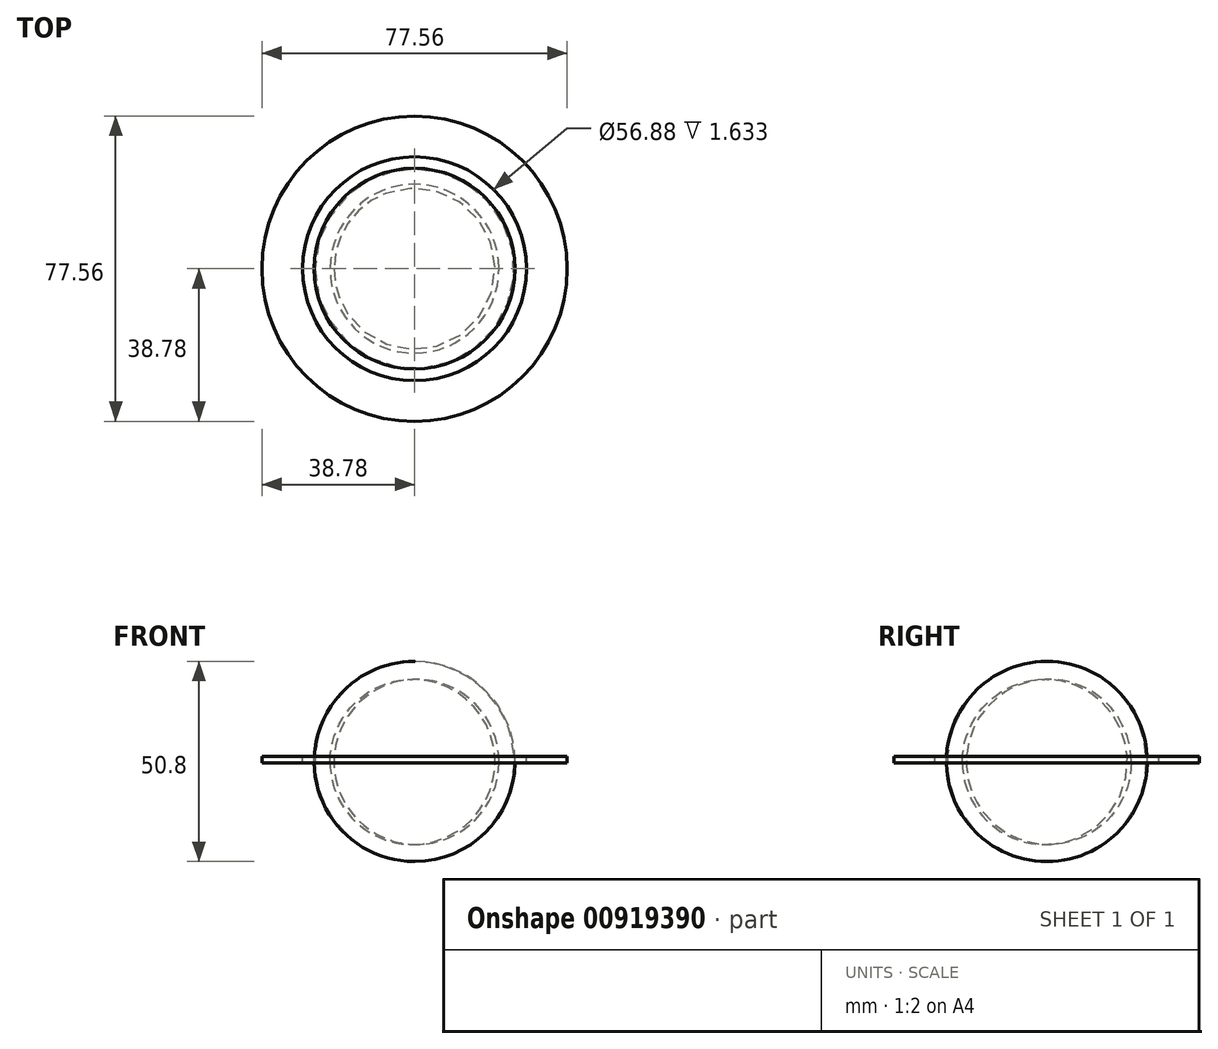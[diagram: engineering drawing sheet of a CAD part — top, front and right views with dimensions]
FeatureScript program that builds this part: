
annotation { "Feature Type Name" : "Feature", "Feature Type Description" : "" }
export const myFeature = defineFeature(function(context is Context, id is Id, definition is map)
    precondition{}
    {
        {
            var Q0;
            Q0=qCreatedBy(makeId("Front.planeOp"),FACE);
            var sketch = newSketch(context, id + "F0", { "sketchPlane" : qUnion([Q0])});
            skArc(sketch, "E0", {"start": v(0, -23.23) * mm, "mid": v(25.29, 2.17) * mm, "end": v(0, 27.57) * mm});
            skLineSegment(sketch, "E1", {"start": v(0, 27.57) * mm, "end": v(0, 23) * mm});
            skLineSegment(sketch, "E2.bottom", {"start": v(38.78, 3.4) * mm, "end": v(28.44, 3.4) * mm});
            skLineSegment(sketch, "E2.top", {"start": v(38.78, 1.77) * mm, "end": v(28.44, 1.77) * mm});
            skLineSegment(sketch, "E2.left", {"start": v(38.78, 3.4) * mm, "end": v(38.78, 1.77) * mm});
            skLineSegment(sketch, "E2.right", {"start": v(28.44, 3.4) * mm, "end": v(28.44, 1.77) * mm});
            skPoint(sketch, "E2.middle", {"position": v(33.6, 2.59) * mm});
            skArc(sketch, "E3", {"start": v(0, -18.91) * mm, "mid": v(20.46, 2.04) * mm, "end": v(0, 23) * mm});
            skLineSegment(sketch, "E4.trimOffspring", {"start": v(0, -18.91) * mm, "end": v(0, -23.23) * mm});
            skLineSegment(sketch, "E5", {"start": v(0, 39.87) * mm, "end": v(0, -37.42) * mm, "construction": true});
            skSolve(sketch);
        }
        {
            var Q0;
            Q0 = qSketchRegion(id + "F0", true);
            var Q1;
            Q1=sQuery(id+"F0.wireOp",EDGE,"E5");
            revolve(context, id + "F1", {"surfaceOperationType" : NewSurfaceOperationType.NEW, "entities" : qUnion([Q0]), "axis" : qUnion([Q1]), "revolveType" : RevolveType.FULL});
        }
    });
